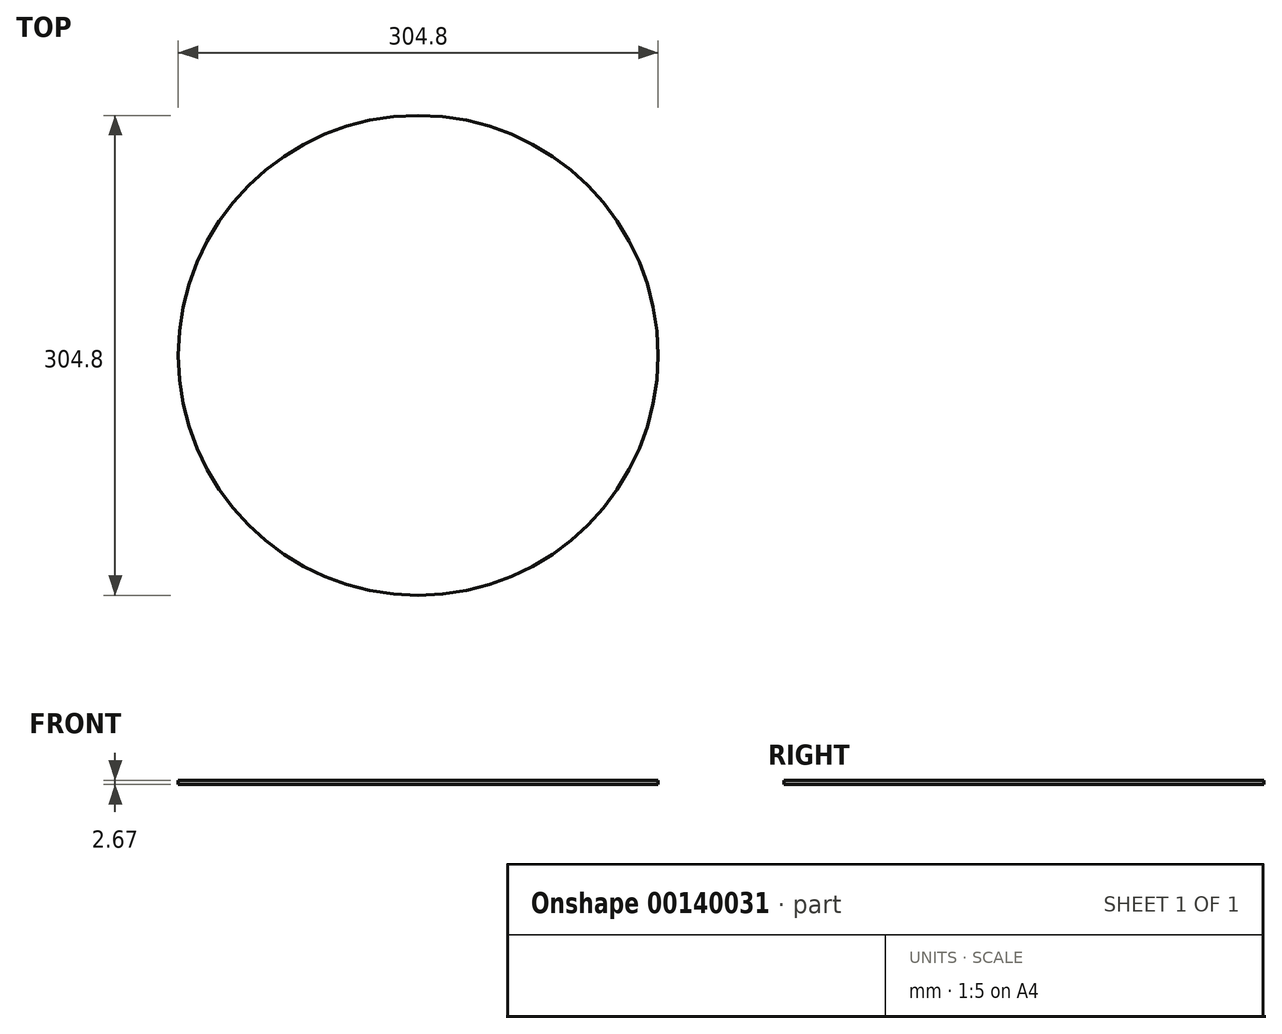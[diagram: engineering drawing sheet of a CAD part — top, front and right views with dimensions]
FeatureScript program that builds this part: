
annotation { "Feature Type Name" : "Feature", "Feature Type Description" : "" }
export const myFeature = defineFeature(function(context is Context, id is Id, definition is map)
    precondition{}
    {
        {
            var Q0;
            Q0=qCreatedBy(makeId("Top.planeOp"),FACE);
            var sketch = newSketch(context, id + "F0", { "sketchPlane" : qUnion([Q0])});
            skCircle(sketch, "E0", {"center": v(0.29, 0) * mm, "radius": 152.4 * mm});
            skSolve(sketch);
        }
        {
            var Q0;
            Q0=qCreatedBy(makeId("Front.planeOp"),FACE);
            var sketch = newSketch(context, id + "F1", { "sketchPlane" : qUnion([Q0])});
            skLineSegment(sketch, "E1", {"start": v(-151.56, 0) * mm, "end": v(-151.56, 355.6) * mm});
            skLineSegment(sketch, "E2", {"start": v(152.4, 0) * mm, "end": v(152.4, 355.6) * mm});
            skLineSegment(sketch, "E3", {"start": v(0, 0) * mm, "end": v(0, 2.67) * mm});
            skLineSegment(sketch, "E4", {"start": v(-151.56, 0) * mm, "end": v(152.4, 0) * mm});
            skLineSegment(sketch, "E5", {"start": v(0, 0) * mm, "end": v(0, 355.6) * mm});
            skLineSegment(sketch, "E6", {"start": v(0, 355.6) * mm, "end": v(-254, 355.6) * mm});
            skLineSegment(sketch, "E7", {"start": v(-254, 355.6) * mm, "end": v(-254, 609.6) * mm});
            skLineSegment(sketch, "E8", {"start": v(152.4, 355.6) * mm, "end": v(254, 355.6) * mm});
            skLineSegment(sketch, "E9", {"start": v(254, 355.6) * mm, "end": v(254, 609.6) * mm});
            skSolve(sketch);
        }
        {
            var Q0;
            Q0=makeQuery(id+"F0.imprint","IMPRINT",FACE,{"disambiguationData":[TD([[makeQuery(id+"F0.imprint","IMPRINT",EDGE,{"derivedFrom":sQuery(id+"F0.wireOp",EDGE,"E0")}),1.0]])]});
            var Q1;
            Q1=sQuery(id+"F0.wireOp",EDGE,"E0");
            var Q2;
            Q2=sQuery(id+"F1.wireOp",EDGE,"E3");
            sweep(context, id + "F2", {"profiles" : qUnion([Q0]), "surfaceProfiles" : qUnion([Q1]), "path" : qUnion([Q2]), "keepProfileOrientation" : true});
        }
        {
            var Q0;
            Q0=sQuery(id+"F1.wireOp",EDGE,"E6");
            var Q1;
            Q1=sQuery(id+"F1.wireOp",EDGE,"E5");
            revolve(context, id + "F3", {"bodyType" : ToolBodyType.SURFACE, "operationType" : NewBodyOperationType.ADD, "surfaceEntities" : qUnion([Q0]), "axis" : qUnion([Q1]), "revolveType" : RevolveType.FULL});
        }
        {
            var Q0;
            Q0=sQuery(id+"F1.wireOp",EDGE,"E7");
            var Q1;
            Q1=makeQuery(id+"F3.opRevolve","SWEPT_EDGE",EDGE,{"disambiguationData":[OSD([sQuery(id+"F1.wireOp",VERTEX,"E6.end")])]});
            revolve(context, id + "F4", {"bodyType" : ToolBodyType.SURFACE, "operationType" : NewBodyOperationType.INTERSECT, "surfaceEntities" : qUnion([Q0]), "axis" : qUnion([Q1]), "revolveType" : RevolveType.FULL});
        }
    });
